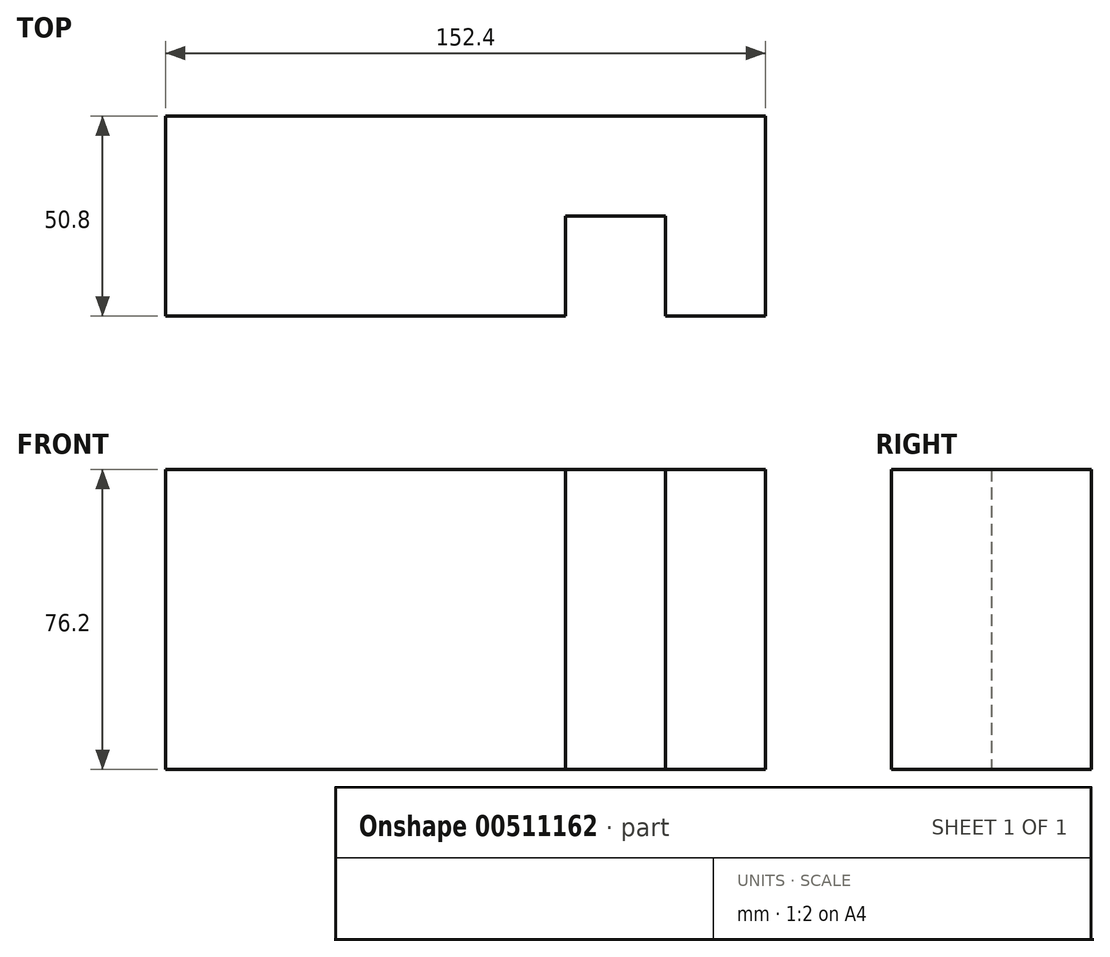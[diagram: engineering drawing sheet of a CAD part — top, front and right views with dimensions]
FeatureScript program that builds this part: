
annotation { "Feature Type Name" : "Feature", "Feature Type Description" : "" }
export const myFeature = defineFeature(function(context is Context, id is Id, definition is map)
    precondition{}
    {
        {
            var Q0;
            Q0=qCreatedBy(makeId("Front.planeOp"),FACE);
            var sketch = newSketch(context, id + "F0", { "sketchPlane" : qUnion([Q0])});
            skLineSegment(sketch, "E0.bottom", {"start": v(-61.82, 51) * mm, "end": v(39.78, 51) * mm});
            skLineSegment(sketch, "E0.top", {"start": v(-61.82, -25.2) * mm, "end": v(39.78, -25.2) * mm});
            skLineSegment(sketch, "E0.left", {"start": v(-61.82, 51) * mm, "end": v(-61.82, -25.2) * mm});
            skLineSegment(sketch, "E0.right", {"start": v(39.78, 51) * mm, "end": v(39.78, -25.2) * mm});
            skLineSegment(sketch, "E1.bottom", {"start": v(39.78, 51) * mm, "end": v(65.18, 51) * mm});
            skLineSegment(sketch, "E1.top", {"start": v(39.78, -25.2) * mm, "end": v(65.18, -25.2) * mm});
            skLineSegment(sketch, "E1.right", {"start": v(65.18, 51) * mm, "end": v(65.18, -25.2) * mm});
            skLineSegment(sketch, "E2.bottom", {"start": v(65.18, 51) * mm, "end": v(90.58, 51) * mm});
            skLineSegment(sketch, "E2.top", {"start": v(65.18, -25.2) * mm, "end": v(90.58, -25.2) * mm});
            skLineSegment(sketch, "E2.right", {"start": v(90.58, 51) * mm, "end": v(90.58, -25.2) * mm});
            skSolve(sketch);
        }
        {
            var Q0;
            Q0=makeQuery(id+"F0.imprint","IMPRINT",FACE,{"disambiguationData":[TD([[makeQuery(id+"F0.imprint","IMPRINT",EDGE,{"derivedFrom":sQuery(id+"F0.wireOp",EDGE,"E1.bottom")}),-1.0]])]});
            extrude(context, id + "F1", {"entities" : qUnion([Q0]), "depth" : 25.4 * mm});
        }
        {
            var Q0;
            Q0=makeQuery(id+"F0.imprint","IMPRINT",FACE,{"disambiguationData":[TD([[makeQuery(id+"F0.imprint","IMPRINT",EDGE,{"derivedFrom":sQuery(id+"F0.wireOp",EDGE,"E0.bottom")}),-1.0]])]});
            var Q1;
            Q1=makeQuery(id+"F0.imprint","IMPRINT",FACE,{"disambiguationData":[TD([[makeQuery(id+"F0.imprint","IMPRINT",EDGE,{"derivedFrom":sQuery(id+"F0.wireOp",EDGE,"E2.bottom")}),-1.0]])]});
            extrude(context, id + "F2", {"entities" : qUnion([Q0, Q1]), "operationType" : NewBodyOperationType.ADD, "depth" : 50.8 * mm});
        }
    });
